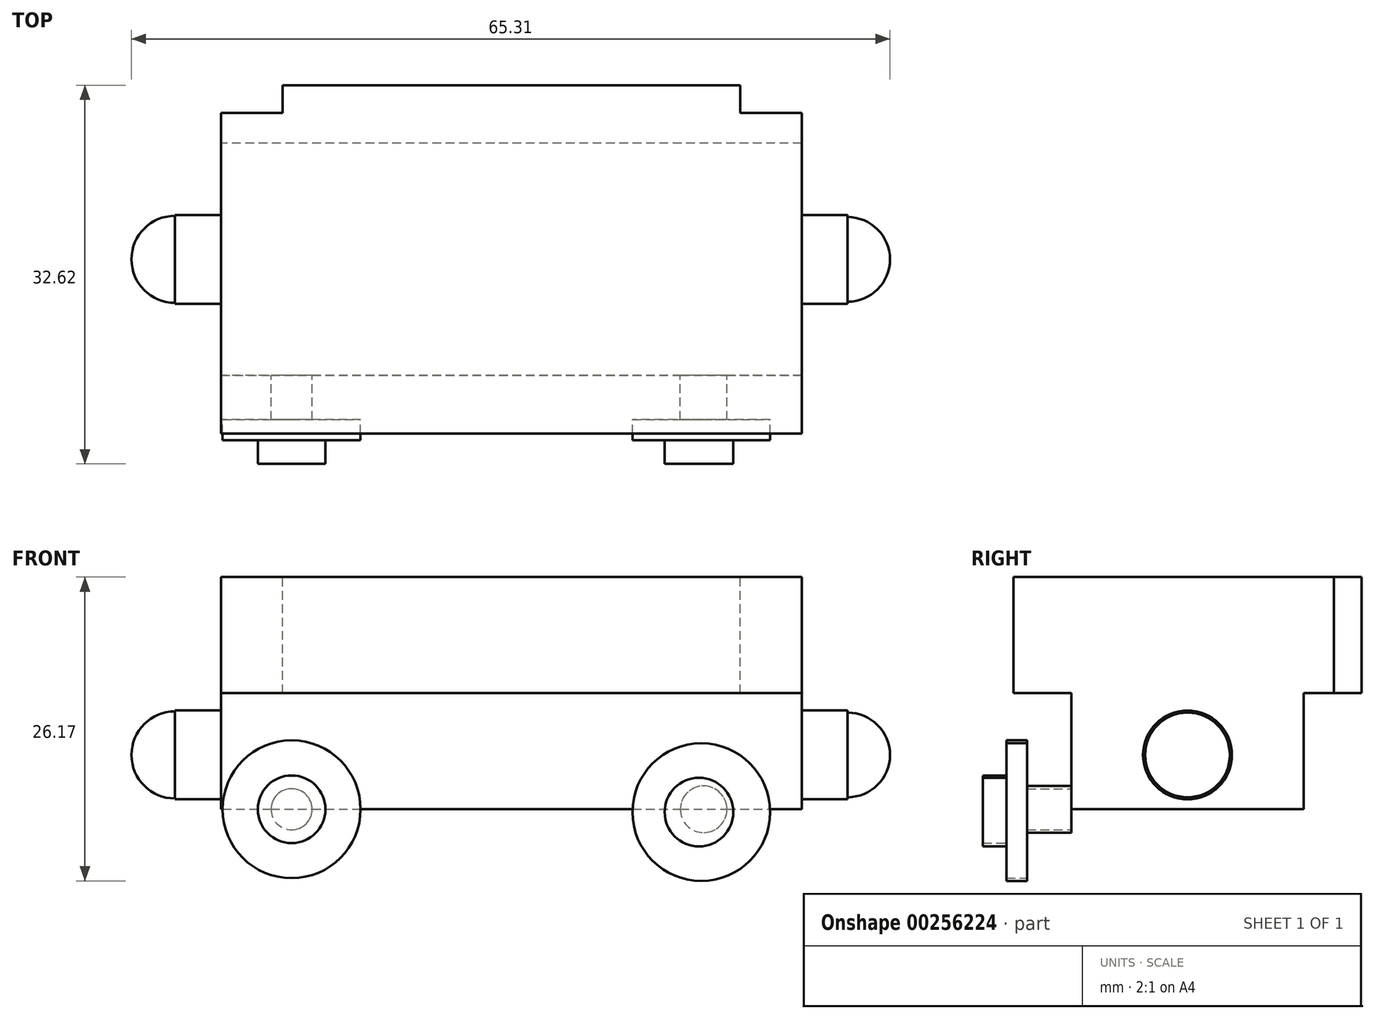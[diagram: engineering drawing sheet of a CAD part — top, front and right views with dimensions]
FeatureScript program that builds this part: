
annotation { "Feature Type Name" : "Feature", "Feature Type Description" : "" }
export const myFeature = defineFeature(function(context is Context, id is Id, definition is map)
    precondition{}
    {
        {
            var Q0;
            Q0=qCreatedBy(makeId("Front.planeOp"),FACE);
            var sketch = newSketch(context, id + "F0", { "sketchPlane" : qUnion([Q0])});
            skLineSegment(sketch, "E0.bottom", {"start": v(-25, 10) * mm, "end": v(25, 10) * mm});
            skLineSegment(sketch, "E0.top", {"start": v(-25, -10) * mm, "end": v(25, -10) * mm});
            skLineSegment(sketch, "E0.left", {"start": v(-25, 10) * mm, "end": v(-25, -10) * mm});
            skLineSegment(sketch, "E0.right", {"start": v(25, 10) * mm, "end": v(25, -10) * mm});
            skPoint(sketch, "E0.middle", {"position": v(0, 0) * mm});
            skSolve(sketch);
        }
        {
            var Q0;
            Q0 = qSketchRegion(id + "F0", true);
            extrude(context, id + "F1", {"entities" : qUnion([Q0]), "endBound" : BoundingType.SYMMETRIC, "depth" : 20 * mm});
        }
        {
            var Q0;
            Q0=qCreatedBy(makeId("Top.planeOp"),FACE);
            var sketch = newSketch(context, id + "F2", { "sketchPlane" : qUnion([Q0])});
            skLineSegment(sketch, "E1.bottom", {"start": v(-25, 15) * mm, "end": v(25, 15) * mm});
            skLineSegment(sketch, "E1.top", {"start": v(-25, -15) * mm, "end": v(25, -15) * mm});
            skLineSegment(sketch, "E1.left", {"start": v(-25, 15) * mm, "end": v(-25, -15) * mm});
            skLineSegment(sketch, "E1.right", {"start": v(25, 15) * mm, "end": v(25, -15) * mm});
            skPoint(sketch, "E1.middle", {"position": v(0, 0) * mm});
            skSolve(sketch);
        }
        {
            var Q0;
            Q0 = qSketchRegion(id + "F2", true);
            extrude(context, id + "F3", {"entities" : qUnion([Q0]), "operationType" : NewBodyOperationType.ADD, "depth" : 10 * mm});
        }
        {
            var Q0;
            Q0=qCreatedBy(makeId("Right.planeOp"),FACE);
            var sketch = newSketch(context, id + "F4", { "sketchPlane" : qUnion([Q0])});
            skCircle(sketch, "E2", {"center": v(0, -5.32) * mm, "radius": 3.83 * mm});
            skSolve(sketch);
        }
        {
            var Q0;
            Q0 = qSketchRegion(id + "F4", true);
            extrude(context, id + "F5", {"entities" : qUnion([Q0]), "operationType" : NewBodyOperationType.ADD, "endBound" : BoundingType.SYMMETRIC, "depth" : 57.9 * mm});
        }
        {
            var Q0;
            Q0=makeQuery(id+"F5.opExtrude","CAP_FACE",FACE,{"disambiguationData":[OSD([sQuery(id+"F4.wireOp",EDGE,"E2")])],"isStart":true});
            var sketch = newSketch(context, id + "F6", { "sketchPlane" : qUnion([Q0])});
            skArc(sketch, "E3", {"start": v(0, -9.07) * mm, "mid": v(3.75, -5.32) * mm, "end": v(0, -1.57) * mm});
            skLineSegment(sketch, "E4", {"start": v(0, -1.5) * mm, "end": v(0, -9.07) * mm});
            skSolve(sketch);
        }
        {
            var Q0;
            Q0 = qSketchRegion(id + "F6", true);
            var Q1;
            Q1=sQuery(id+"F6.wireOp",EDGE,"E4");
            revolve(context, id + "F7", {"operationType" : NewBodyOperationType.ADD, "entities" : qUnion([Q0]), "axis" : qUnion([Q1]), "revolveType" : RevolveType.FULL});
        }
        {
            var Q0;
            Q0=makeQuery(id+"F5.opExtrude","CAP_FACE",FACE,{"disambiguationData":[OSD([sQuery(id+"F4.wireOp",EDGE,"E2")])],"isStart":false});
            var sketch = newSketch(context, id + "F8", { "sketchPlane" : qUnion([Q0])});
            skArc(sketch, "E5", {"start": v(0, -8.97) * mm, "mid": v(3.65, -5.32) * mm, "end": v(0, -1.67) * mm});
            skLineSegment(sketch, "E6", {"start": v(0, -1.5) * mm, "end": v(0, -9.15) * mm});
            skSolve(sketch);
        }
        {
            var Q0;
            Q0 = qSketchRegion(id + "F8", true);
            var Q1;
            Q1=sQuery(id+"F8.wireOp",EDGE,"E6");
            revolve(context, id + "F9", {"operationType" : NewBodyOperationType.ADD, "entities" : qUnion([Q0]), "axis" : qUnion([Q1]), "revolveType" : RevolveType.FULL});
        }
        {
            var Q0;
            Q0=makeQuery(id+"F3.opExtrude","CAP_FACE",FACE,{"disambiguationData":[OSD([sQuery(id+"F2.wireOp",EDGE,"E1.bottom"),sQuery(id+"F2.wireOp",EDGE,"E1.top"),sQuery(id+"F2.wireOp",EDGE,"E1.left"),sQuery(id+"F2.wireOp",EDGE,"E1.right")])],"isStart":false});
            var sketch = newSketch(context, id + "F10", { "sketchPlane" : qUnion([Q0])});
            skLineSegment(sketch, "E7.bottom", {"start": v(-25, 15) * mm, "end": v(-19.7, 15) * mm});
            skLineSegment(sketch, "E7.top", {"start": v(-25, 12.61) * mm, "end": v(-19.7, 12.61) * mm});
            skLineSegment(sketch, "E7.left", {"start": v(-25, 15) * mm, "end": v(-25, 12.61) * mm});
            skLineSegment(sketch, "E7.right", {"start": v(-19.7, 15) * mm, "end": v(-19.7, 12.61) * mm});
            skLineSegment(sketch, "E8.bottom", {"start": v(25, 15) * mm, "end": v(19.7, 15) * mm});
            skLineSegment(sketch, "E8.top", {"start": v(25, 12.61) * mm, "end": v(19.7, 12.61) * mm});
            skLineSegment(sketch, "E8.left", {"start": v(25, 15) * mm, "end": v(25, 12.61) * mm});
            skLineSegment(sketch, "E8.right", {"start": v(19.7, 15) * mm, "end": v(19.7, 12.61) * mm});
            skSolve(sketch);
        }
        {
            var Q0;
            Q0 = qSketchRegion(id + "F10", true);
            extrude(context, id + "F11", {"entities" : qUnion([Q0]), "operationType" : NewBodyOperationType.REMOVE, "endBound" : BoundingType.THROUGH_ALL, "oppositeDirection" : true, "depth" : 30.48 * mm});
        }
        {
            var Q0;
            Q0=makeQuery(id+"F1.opExtrude","CAP_FACE",FACE,{"disambiguationData":[OSD([sQuery(id+"F0.wireOp",EDGE,"E0.bottom"),sQuery(id+"F0.wireOp",EDGE,"E0.top"),sQuery(id+"F0.wireOp",EDGE,"E0.left"),sQuery(id+"F0.wireOp",EDGE,"E0.right")])],"isStart":false});
            var sketch = newSketch(context, id + "F12", { "sketchPlane" : qUnion([Q0])});
            skPoint(sketch, "E9.centerSnap0", {"position": v(-25, -5) * mm});
            skPoint(sketch, "E10.centerSnap0", {"position": v(25, -5) * mm});
            skCircle(sketch, "E11", {"center": v(-18.92, -10) * mm, "radius": 1.77 * mm});
            skCircle(sketch, "E12", {"center": v(16.55, -10) * mm, "radius": 2 * mm});
            skSolve(sketch);
        }
        {
            var Q0;
            Q0 = qSketchRegion(id + "F12", true);
            extrude(context, id + "F13", {"entities" : qUnion([Q0]), "operationType" : NewBodyOperationType.ADD, "depth" : 3.8 * mm});
        }
        {
            var Q0;
            Q0=makeQuery(id+"F13.opExtrude","CAP_FACE",FACE,{"disambiguationData":[OSD([sQuery(id+"F12.wireOp",EDGE,"E11")])],"isStart":false});
            var sketch = newSketch(context, id + "F14", { "sketchPlane" : qUnion([Q0])});
            skCircle(sketch, "E13", {"center": v(-18.92, -10) * mm, "radius": 5.94 * mm});
            skCircle(sketch, "E14", {"center": v(16.36, -10.25) * mm, "radius": 5.93 * mm});
            skSolve(sketch);
        }
        {
            var Q0;
            Q0 = qSketchRegion(id + "F14", true);
            extrude(context, id + "F15", {"entities" : qUnion([Q0]), "operationType" : NewBodyOperationType.ADD, "depth" : 1.78 * mm});
        }
        {
            var Q0;
            Q0=makeQuery(id+"F15.opExtrude","CAP_FACE",FACE,{"disambiguationData":[OSD([sQuery(id+"F14.wireOp",EDGE,"E13")])],"isStart":false});
            var sketch = newSketch(context, id + "F16", { "sketchPlane" : qUnion([Q0])});
            skCircle(sketch, "E15", {"center": v(-18.92, -10) * mm, "radius": 2.91 * mm});
            skCircle(sketch, "E16", {"center": v(16.16, -10.25) * mm, "radius": 2.96 * mm});
            skSolve(sketch);
        }
        {
            var Q0;
            Q0 = qSketchRegion(id + "F16", true);
            extrude(context, id + "F17", {"entities" : qUnion([Q0]), "operationType" : NewBodyOperationType.ADD, "depth" : 2.03 * mm});
        }
    });
